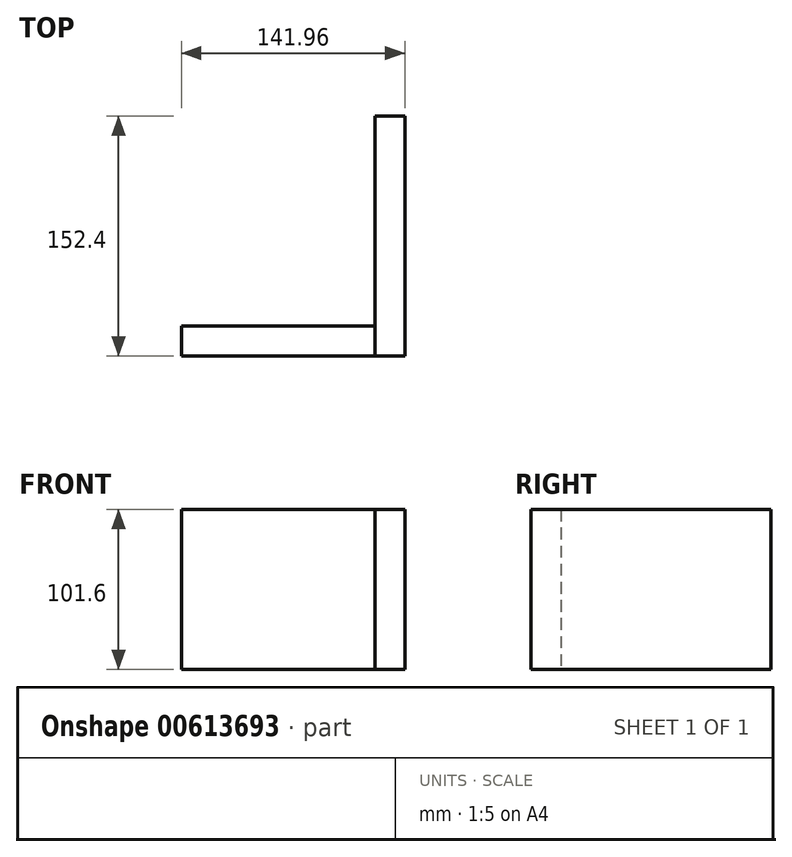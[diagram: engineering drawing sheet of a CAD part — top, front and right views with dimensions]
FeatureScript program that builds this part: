
annotation { "Feature Type Name" : "Feature", "Feature Type Description" : "" }
export const myFeature = defineFeature(function(context is Context, id is Id, definition is map)
    precondition{}
    {
        {
            var Q0;
            Q0=qCreatedBy(makeId("Top.planeOp"),FACE);
            var sketch = newSketch(context, id + "F0", { "sketchPlane" : qUnion([Q0])});
            skLineSegment(sketch, "E0.bottom", {"start": v(0, 0) * mm, "end": v(-122.9, 0) * mm});
            skLineSegment(sketch, "E0.top", {"start": v(0, 19.05) * mm, "end": v(-122.9, 19.05) * mm});
            skLineSegment(sketch, "E0.left", {"start": v(0, 0) * mm, "end": v(0, 19.05) * mm});
            skLineSegment(sketch, "E0.right", {"start": v(-122.9, 0) * mm, "end": v(-122.9, 19.05) * mm});
            skLineSegment(sketch, "E1.bottom", {"start": v(0, 0) * mm, "end": v(19.05, 0) * mm});
            skLineSegment(sketch, "E1.top", {"start": v(0, 152.4) * mm, "end": v(19.05, 152.4) * mm});
            skLineSegment(sketch, "E1.left", {"start": v(0, 0) * mm, "end": v(0, 152.4) * mm});
            skLineSegment(sketch, "E1.right", {"start": v(19.05, 0) * mm, "end": v(19.05, 152.4) * mm});
            skSolve(sketch);
        }
        {
            var Q0;
            {var subQ0=sQuery(id+"F0.wireOp",EDGE,"E0.bottom");Q0=makeQuery(id+"F0.imprint","IMPRINT",FACE,{"disambiguationData":[TD([[makeQuery(id+"F0.imprint","IMPRINT",EDGE,{"derivedFrom":subQ0}),-1.0]])]});}
            extrude(context, id + "F1", {"entities" : qUnion([Q0]), "depth" : 101.6 * mm, "offsetDistance" : 25.4 * mm});
        }
        {
            var Q0;
            {var subQ3=sQuery(id+"F0.wireOp",EDGE,"E1.bottom");Q0=makeQuery(id+"F0.imprint","IMPRINT",FACE,{"disambiguationData":[TD([[makeQuery(id+"F0.imprint","IMPRINT",EDGE,{"derivedFrom":subQ3}),1.0]])]});}
            extrude(context, id + "F2", {"entities" : qUnion([Q0]), "depth" : 101.6 * mm, "offsetDistance" : 25.4 * mm});
        }
    });
